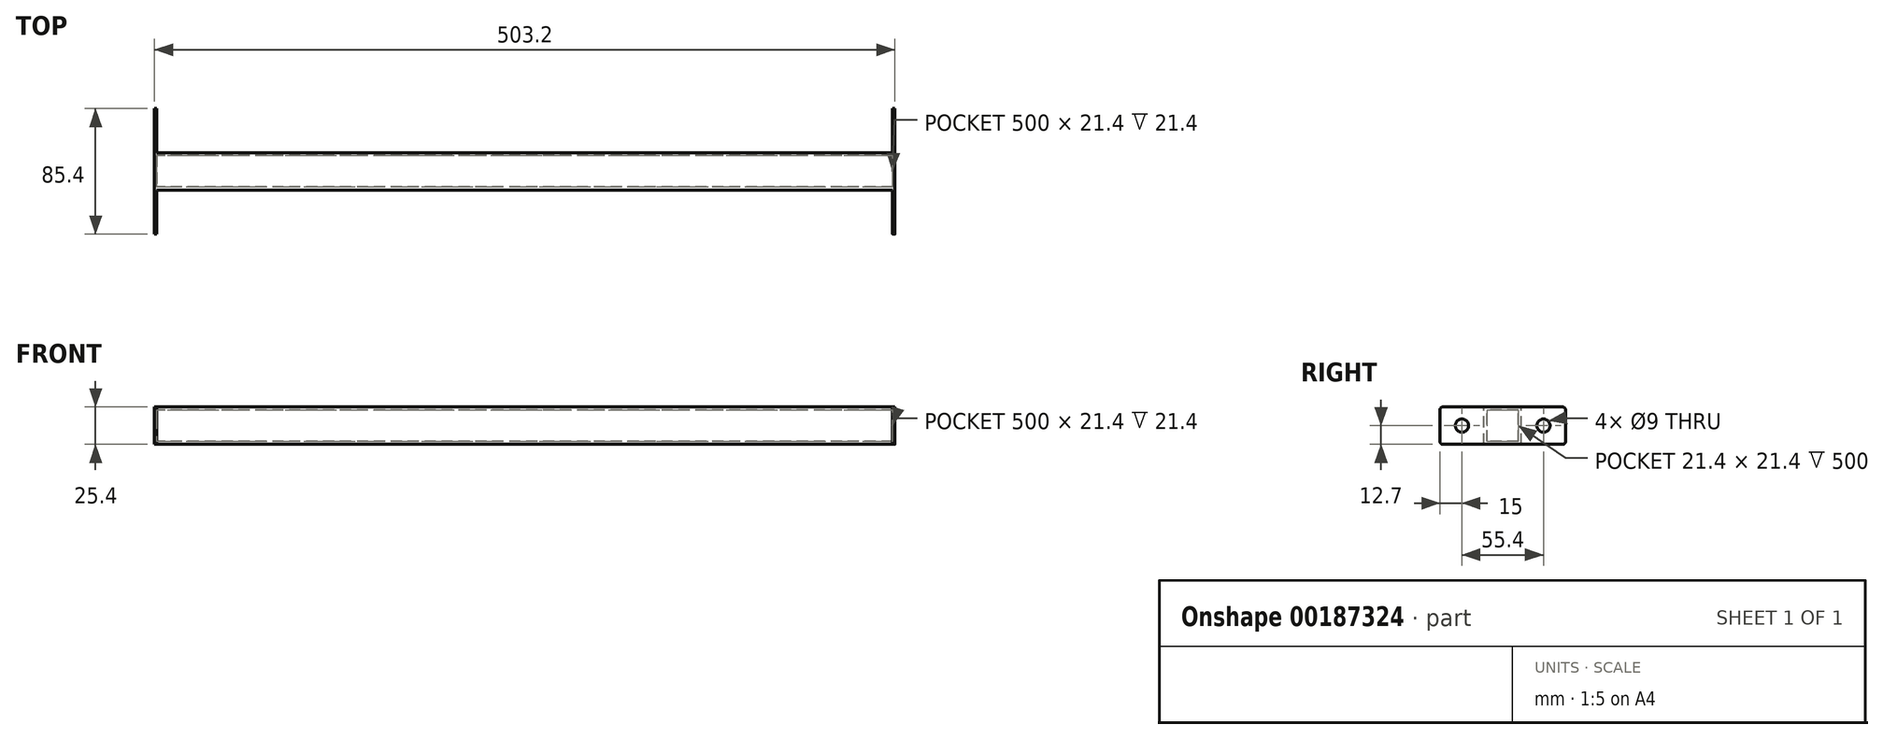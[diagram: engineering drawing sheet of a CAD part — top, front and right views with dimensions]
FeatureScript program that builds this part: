
annotation { "Feature Type Name" : "Feature", "Feature Type Description" : "" }
export const myFeature = defineFeature(function(context is Context, id is Id, definition is map)
    precondition{}
    {
        {
            var Q0;
            Q0=qCreatedBy(makeId("Right.planeOp"),FACE);
            var sketch = newSketch(context, id + "F0", { "sketchPlane" : qUnion([Q0])});
            skLineSegment(sketch, "E0.bottom", {"start": v(12.7, -12.7) * mm, "end": v(-12.7, -12.7) * mm});
            skLineSegment(sketch, "E0.top", {"start": v(12.7, 12.7) * mm, "end": v(-12.7, 12.7) * mm});
            skLineSegment(sketch, "E0.left", {"start": v(12.7, -12.7) * mm, "end": v(12.7, 12.7) * mm});
            skLineSegment(sketch, "E0.right", {"start": v(-12.7, -12.7) * mm, "end": v(-12.7, 12.7) * mm});
            skPoint(sketch, "E0.middle", {"position": v(0, 0) * mm});
            skSolve(sketch);
        }
        {
            var Q0;
            Q0 = qSketchRegion(id + "F0", true);
            extrude(context, id + "F1", {"entities" : qUnion([Q0]), "endBound" : BoundingType.SYMMETRIC, "depth" : 500 * mm});
        }
        {
            var Q0;
            Q0=makeQuery(id+"F1.opExtrude","CAP_FACE",FACE,{"disambiguationData":[OSD([sQuery(id+"F0.wireOp",EDGE,"E0.bottom"),sQuery(id+"F0.wireOp",EDGE,"E0.top"),sQuery(id+"F0.wireOp",EDGE,"E0.left"),sQuery(id+"F0.wireOp",EDGE,"E0.right")])],"isStart":false});
            var Q1;
            Q1=makeQuery(id+"F1.opExtrude","CAP_FACE",FACE,{"disambiguationData":[OSD([sQuery(id+"F0.wireOp",EDGE,"E0.bottom"),sQuery(id+"F0.wireOp",EDGE,"E0.top"),sQuery(id+"F0.wireOp",EDGE,"E0.left"),sQuery(id+"F0.wireOp",EDGE,"E0.right")])],"isStart":true});
            shell(context, id + "F2", {"entities" : qUnion([Q0, Q1]), "thickness" : 2 * mm});
        }
        {
            var Q0;
            Q0=makeQuery(id+"F1.opExtrude","CAP_FACE",FACE,{"disambiguationData":[OSD([sQuery(id+"F0.wireOp",EDGE,"E0.bottom"),sQuery(id+"F0.wireOp",EDGE,"E0.top"),sQuery(id+"F0.wireOp",EDGE,"E0.left"),sQuery(id+"F0.wireOp",EDGE,"E0.right")])],"isStart":false});
            var sketch = newSketch(context, id + "F3", { "sketchPlane" : qUnion([Q0])});
            skLineSegment(sketch, "E1.0", {"start": v(40.7, 12.7) * mm, "end": v(-40.7, 12.7) * mm});
            skLineSegment(sketch, "E2.0", {"start": v(40.7, -12.7) * mm, "end": v(-40.7, -12.7) * mm});
            skLineSegment(sketch, "E3.0", {"start": v(42.7, -10.7) * mm, "end": v(42.7, 10.7) * mm});
            skLineSegment(sketch, "E4.0", {"start": v(-42.7, -10.7) * mm, "end": v(-42.7, 10.7) * mm});
            skPoint(sketch, "E5.0.end.orphan", {"position": v(-12.7, 12.7) * mm});
            skPoint(sketch, "E5.0.start.orphan", {"position": v(-12.7, -12.7) * mm});
            skPoint(sketch, "E6.0.end.orphan", {"position": v(12.7, 12.7) * mm});
            skPoint(sketch, "E6.0.start.orphan", {"position": v(12.7, -12.7) * mm});
            skPoint(sketch, "E7.visualSharp", {"position": v(-42.7, 12.7) * mm});
            skArc(sketch, "E7.filletArc", {"start": v(-40.7, 12.7) * mm, "mid": v(-42.11, 12.11) * mm, "end": v(-42.7, 10.7) * mm});
            skPoint(sketch, "E8.visualSharp", {"position": v(-42.7, -12.7) * mm});
            skArc(sketch, "E8.filletArc", {"start": v(-42.7, -10.7) * mm, "mid": v(-42.11, -12.11) * mm, "end": v(-40.7, -12.7) * mm});
            skPoint(sketch, "E9.visualSharp", {"position": v(42.7, -12.7) * mm});
            skArc(sketch, "E9.filletArc", {"start": v(40.7, -12.7) * mm, "mid": v(42.11, -12.11) * mm, "end": v(42.7, -10.7) * mm});
            skPoint(sketch, "E10.visualSharp", {"position": v(42.7, 12.7) * mm});
            skArc(sketch, "E10.filletArc", {"start": v(42.7, 10.7) * mm, "mid": v(42.11, 12.11) * mm, "end": v(40.7, 12.7) * mm});
            skCircle(sketch, "E11", {"center": v(-27.7, 0) * mm, "radius": 4.5 * mm});
            skCircle(sketch, "E12", {"center": v(27.7, 0) * mm, "radius": 4.5 * mm});
            skSolve(sketch);
        }
        {
            var Q0;
            Q0 = qSketchRegion(id + "F3", true);
            extrude(context, id + "F4", {"entities" : qUnion([Q0]), "operationType" : NewBodyOperationType.ADD, "depth" : 1.6 * mm});
        }
        {
            var Q0;
            Q0=makeQuery(id+"F1.opExtrude","CAP_FACE",FACE,{"disambiguationData":[OSD([sQuery(id+"F0.wireOp",EDGE,"E0.bottom"),sQuery(id+"F0.wireOp",EDGE,"E0.top"),sQuery(id+"F0.wireOp",EDGE,"E0.left"),sQuery(id+"F0.wireOp",EDGE,"E0.right")])],"isStart":true});
            var sketch = newSketch(context, id + "F5", { "sketchPlane" : qUnion([Q0])});
            skLineSegment(sketch, "E13.0", {"start": v(-40.7, 12.7) * mm, "end": v(-12.7, 12.7) * mm});
            skArc(sketch, "E13.1", {"start": v(-42.7, 10.7) * mm, "mid": v(-42.11, 12.11) * mm, "end": v(-40.7, 12.7) * mm});
            skLineSegment(sketch, "E13.2.0", {"start": v(-40.7, -12.7) * mm, "end": v(-12.7, -12.7) * mm});
            skLineSegment(sketch, "E13.2.1", {"start": v(-12.7, -12.7) * mm, "end": v(-12.7, 12.7) * mm});
            skLineSegment(sketch, "E13.2.2", {"start": v(-12.7, 12.7) * mm, "end": v(-40.7, 12.7) * mm});
            skArc(sketch, "E13.2.3", {"start": v(-40.7, 12.7) * mm, "mid": v(-42.11, 12.11) * mm, "end": v(-42.7, 10.7) * mm});
            skLineSegment(sketch, "E13.2.4", {"start": v(-42.7, 10.7) * mm, "end": v(-42.7, -10.7) * mm});
            skArc(sketch, "E13.2.5", {"start": v(-42.7, -10.7) * mm, "mid": v(-42.11, -12.11) * mm, "end": v(-40.7, -12.7) * mm});
            skLineSegment(sketch, "E13.3", {"start": v(-12.7, -12.7) * mm, "end": v(12.7, -12.7) * mm});
            skLineSegment(sketch, "E13.4", {"start": v(12.7, -12.7) * mm, "end": v(40.7, -12.7) * mm});
            skArc(sketch, "E13.5", {"start": v(42.7, -10.7) * mm, "mid": v(42.11, -12.11) * mm, "end": v(40.7, -12.7) * mm});
            skLineSegment(sketch, "E13.6", {"start": v(42.7, -10.7) * mm, "end": v(42.7, 10.7) * mm});
            skArc(sketch, "E13.7", {"start": v(40.7, 12.7) * mm, "mid": v(42.11, 12.11) * mm, "end": v(42.7, 10.7) * mm});
            skLineSegment(sketch, "E13.8", {"start": v(12.7, 12.7) * mm, "end": v(40.7, 12.7) * mm});
            skLineSegment(sketch, "E13.9", {"start": v(-12.7, 12.7) * mm, "end": v(12.7, 12.7) * mm});
            skCircle(sketch, "E13.10", {"center": v(27.7, 0) * mm, "radius": 4.5 * mm});
            skCircle(sketch, "E14.0", {"center": v(-27.7, 0) * mm, "radius": 4.5 * mm});
            skSolve(sketch);
        }
        {
            var Q0;
            Q0 = qSketchRegion(id + "F5", true);
            extrude(context, id + "F6", {"entities" : qUnion([Q0]), "operationType" : NewBodyOperationType.ADD, "depth" : 1.6 * mm});
        }
    });
